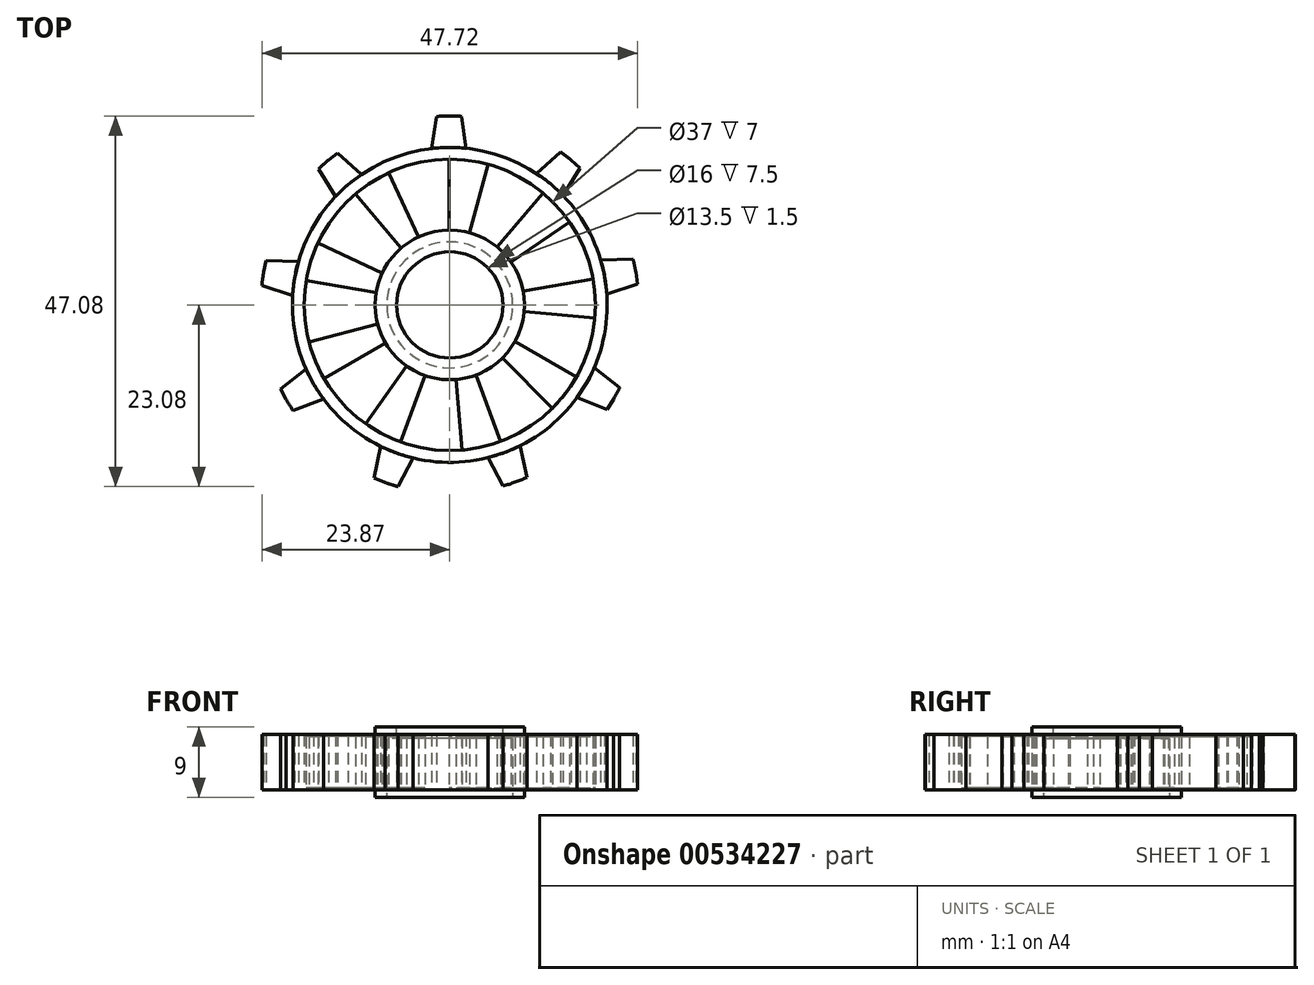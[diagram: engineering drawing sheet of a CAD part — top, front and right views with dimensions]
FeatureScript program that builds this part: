
annotation { "Feature Type Name" : "Feature", "Feature Type Description" : "" }
export const myFeature = defineFeature(function(context is Context, id is Id, definition is map)
    precondition{}
    {
        {
            var Q0;
            Q0=qCreatedBy(makeId("Top.planeOp"),FACE);
            var sketch = newSketch(context, id + "F0", { "sketchPlane" : qUnion([Q0])});
            skCircle(sketch, "E0", {"center": v(0, 0) * mm, "radius": 8 * mm});
            skCircle(sketch, "E1", {"center": v(0, 0) * mm, "radius": 9.5 * mm});
            skCircle(sketch, "E2", {"center": v(0, 0) * mm, "radius": 18.5 * mm});
            skCircle(sketch, "E3", {"center": v(0, 0) * mm, "radius": 20 * mm});
            skCircle(sketch, "E4", {"center": v(0, 0) * mm, "radius": 24 * mm});
            skLineSegment(sketch, "E5.trimOffspring", {"start": v(-0.1, 9.5) * mm, "end": v(-0.1, 18.5) * mm});
            skLineSegment(sketch, "E6", {"start": v(2.5, 9.17) * mm, "end": v(4.86, 17.85) * mm});
            skLineSegment(sketch, "E7.1.0", {"start": v(-6.18, 7.21) * mm, "end": v(-11.97, 14.1) * mm});
            skLineSegment(sketch, "E7.1.1", {"start": v(-3.98, 8.63) * mm, "end": v(-7.75, 16.8) * mm});
            skLineSegment(sketch, "E7.2.0", {"start": v(-9.37, 1.55) * mm, "end": v(-18.24, 3.11) * mm});
            skLineSegment(sketch, "E7.2.1", {"start": v(-8.6, 4.05) * mm, "end": v(-16.74, 7.88) * mm});
            skLineSegment(sketch, "E7.3.0", {"start": v(-8.18, -4.84) * mm, "end": v(-15.97, -9.34) * mm});
            skLineSegment(sketch, "E7.3.1", {"start": v(-9.19, -2.42) * mm, "end": v(-17.89, -4.72) * mm});
            skLineSegment(sketch, "E7.4.0", {"start": v(-3.15, -8.96) * mm, "end": v(-6.23, -17.42) * mm});
            skLineSegment(sketch, "E7.4.1", {"start": v(-5.48, -7.76) * mm, "end": v(-10.67, -15.11) * mm});
            skLineSegment(sketch, "E7.5.0", {"start": v(3.34, -8.9) * mm, "end": v(6.42, -17.35) * mm});
            skLineSegment(sketch, "E7.5.1", {"start": v(0.8, -9.47) * mm, "end": v(1.54, -18.44) * mm});
            skLineSegment(sketch, "E7.6.0", {"start": v(8.28, -4.66) * mm, "end": v(16.07, -9.16) * mm});
            skLineSegment(sketch, "E7.6.1", {"start": v(6.7, -6.74) * mm, "end": v(13.03, -13.13) * mm});
            skLineSegment(sketch, "E7.7.0", {"start": v(9.34, 1.75) * mm, "end": v(18.2, 3.31) * mm});
            skLineSegment(sketch, "E7.7.1", {"start": v(9.46, -0.86) * mm, "end": v(18.42, -1.68) * mm});
            skLineSegment(sketch, "E7.8.0", {"start": v(6.03, 7.34) * mm, "end": v(11.81, 14.24) * mm});
            skLineSegment(sketch, "E7.8.1", {"start": v(7.8, 5.42) * mm, "end": v(15.2, 10.55) * mm});
            skLineSegment(sketch, "E8", {"start": v(-1.7, 23.94) * mm, "end": v(-2.3, 19.87) * mm});
            skLineSegment(sketch, "E9", {"start": v(1.5, 23.95) * mm, "end": v(2.1, 19.89) * mm});
            skLineSegment(sketch, "E10.1.0", {"start": v(-15.57, 18.25) * mm, "end": v(-16.69, 17.25) * mm});
            skLineSegment(sketch, "E10.1.1", {"start": v(-16.69, 17.25) * mm, "end": v(-14.53, 13.74) * mm});
            skLineSegment(sketch, "E10.1.2", {"start": v(-15.43, 18.39) * mm, "end": v(-14.25, 19.31) * mm});
            skLineSegment(sketch, "E10.1.3", {"start": v(-12.92, 15.24) * mm, "end": v(-14.53, 13.74) * mm});
            skLineSegment(sketch, "E10.1.4", {"start": v(-14.25, 19.31) * mm, "end": v(-11.18, 16.58) * mm});
            skLineSegment(sketch, "E10.1.5", {"start": v(-12.93, 15.26) * mm, "end": v(-11.18, 16.58) * mm});
            skLineSegment(sketch, "E10.2.0", {"start": v(-23.66, 3.97) * mm, "end": v(-23.87, 2.48) * mm});
            skLineSegment(sketch, "E10.2.1", {"start": v(-23.87, 2.48) * mm, "end": v(-19.96, 1.19) * mm});
            skLineSegment(sketch, "E10.2.2", {"start": v(-23.64, 4.17) * mm, "end": v(-23.33, 5.64) * mm});
            skLineSegment(sketch, "E10.2.3", {"start": v(-19.7, 3.37) * mm, "end": v(-19.96, 1.19) * mm});
            skLineSegment(sketch, "E10.2.4", {"start": v(-23.33, 5.64) * mm, "end": v(-19.22, 5.52) * mm});
            skLineSegment(sketch, "E10.2.5", {"start": v(-19.71, 3.37) * mm, "end": v(-19.22, 5.52) * mm});
            skLineSegment(sketch, "E10.3.0", {"start": v(-20.67, -12.17) * mm, "end": v(-19.88, -13.44) * mm});
            skLineSegment(sketch, "E10.3.1", {"start": v(-19.88, -13.44) * mm, "end": v(-16.06, -11.92) * mm});
            skLineSegment(sketch, "E10.3.2", {"start": v(-20.78, -12) * mm, "end": v(-21.5, -10.68) * mm});
            skLineSegment(sketch, "E10.3.3", {"start": v(-17.25, -10.07) * mm, "end": v(-16.06, -11.92) * mm});
            skLineSegment(sketch, "E10.3.4", {"start": v(-21.5, -10.68) * mm, "end": v(-18.27, -8.13) * mm});
            skLineSegment(sketch, "E10.3.5", {"start": v(-17.27, -10.09) * mm, "end": v(-18.27, -8.13) * mm});
            skLineSegment(sketch, "E10.4.0", {"start": v(-8.02, -22.6) * mm, "end": v(-6.6, -23.08) * mm});
            skLineSegment(sketch, "E10.4.1", {"start": v(-6.6, -23.08) * mm, "end": v(-4.64, -19.45) * mm});
            skLineSegment(sketch, "E10.4.2", {"start": v(-8.2, -22.55) * mm, "end": v(-9.6, -22) * mm});
            skLineSegment(sketch, "E10.4.3", {"start": v(-6.74, -18.8) * mm, "end": v(-4.64, -19.45) * mm});
            skLineSegment(sketch, "E10.4.4", {"start": v(-9.6, -22) * mm, "end": v(-8.77, -17.97) * mm});
            skLineSegment(sketch, "E10.4.5", {"start": v(-6.75, -18.83) * mm, "end": v(-8.77, -17.97) * mm});
            skLineSegment(sketch, "E10.5.1", {"start": v(9.78, -21.92) * mm, "end": v(8.95, -17.88) * mm});
            skLineSegment(sketch, "E10.5.3", {"start": v(6.93, -18.74) * mm, "end": v(8.95, -17.88) * mm});
            skLineSegment(sketch, "E10.5.4", {"start": v(6.78, -23.02) * mm, "end": v(4.83, -19.4) * mm});
            skLineSegment(sketch, "E10.5.5", {"start": v(6.93, -18.76) * mm, "end": v(4.83, -19.4) * mm});
            skLineSegment(sketch, "E10.6.0", {"start": v(20.87, -11.82) * mm, "end": v(21.58, -10.5) * mm});
            skLineSegment(sketch, "E10.6.1", {"start": v(21.58, -10.5) * mm, "end": v(18.35, -7.95) * mm});
            skLineSegment(sketch, "E10.6.2", {"start": v(20.78, -12) * mm, "end": v(20, -13.27) * mm});
            skLineSegment(sketch, "E10.6.3", {"start": v(17.35, -9.9) * mm, "end": v(18.35, -7.95) * mm});
            skLineSegment(sketch, "E10.6.4", {"start": v(20, -13.27) * mm, "end": v(16.18, -11.76) * mm});
            skLineSegment(sketch, "E10.6.5", {"start": v(17.37, -9.91) * mm, "end": v(16.18, -11.76) * mm});
            skLineSegment(sketch, "E10.7.0", {"start": v(23.59, 4.36) * mm, "end": v(23.28, 5.83) * mm});
            skLineSegment(sketch, "E10.7.1", {"start": v(23.28, 5.83) * mm, "end": v(19.17, 5.71) * mm});
            skLineSegment(sketch, "E10.7.2", {"start": v(23.64, 4.17) * mm, "end": v(23.85, 2.68) * mm});
            skLineSegment(sketch, "E10.7.3", {"start": v(19.66, 3.57) * mm, "end": v(19.17, 5.71) * mm});
            skLineSegment(sketch, "E10.7.4", {"start": v(23.85, 2.68) * mm, "end": v(19.95, 1.39) * mm});
            skLineSegment(sketch, "E10.7.5", {"start": v(19.68, 3.57) * mm, "end": v(19.95, 1.39) * mm});
            skLineSegment(sketch, "E10.8.0", {"start": v(15.27, 18.5) * mm, "end": v(14.09, 19.43) * mm});
            skLineSegment(sketch, "E10.8.1", {"start": v(14.09, 19.43) * mm, "end": v(11.01, 16.7) * mm});
            skLineSegment(sketch, "E10.8.2", {"start": v(15.43, 18.39) * mm, "end": v(16.55, 17.39) * mm});
            skLineSegment(sketch, "E10.8.3", {"start": v(12.77, 15.37) * mm, "end": v(11.01, 16.7) * mm});
            skLineSegment(sketch, "E10.8.4", {"start": v(16.55, 17.39) * mm, "end": v(14.4, 13.89) * mm});
            skLineSegment(sketch, "E10.8.5", {"start": v(12.78, 15.39) * mm, "end": v(14.4, 13.89) * mm});
            skSolve(sketch);
        }
        {
            var Q0;
            Q0=makeQuery(id+"F0.imprint","IMPRINT",FACE,{"disambiguationData":[TD([[makeQuery(id+"F0.imprint","IMPRINT",EDGE,{"derivedFrom":sQuery(id+"F0.wireOp",EDGE,"E0")}),-1.0]])]});
            extrude(context, id + "F1", {"entities" : qUnion([Q0]), "endBound" : BoundingType.SYMMETRIC, "depth" : 9 * mm, "offsetDistance" : 25 * mm});
        }
        {
            var Q0;
            {var subQ11=sQuery(id+"F0.wireOp",EDGE,"KNoMOfHx-20VM-SqMY-RUze-EZyGc1flUTZU");Q0=makeQuery(id+"F0.imprint","IMPRINT",FACE,{"disambiguationData":[TD([[makeQuery(id+"F0.imprint","IMPRINT",EDGE,{"derivedFrom":subQ11}),-1.0]])]});}
            var Q1;
            {var subQ0=sQuery(id+"F0.wireOp",EDGE,"E7.1.0");Q1=makeQuery(id+"F0.imprint","IMPRINT",FACE,{"disambiguationData":[TD([[makeQuery(id+"F0.imprint","IMPRINT",EDGE,{"derivedFrom":subQ0}),-1.0]])]});}
            var Q2;
            {var subQ0=sQuery(id+"F0.wireOp",EDGE,"E5.trimOffspring");Q2=makeQuery(id+"F0.imprint","IMPRINT",FACE,{"disambiguationData":[TD([[makeQuery(id+"F0.imprint","IMPRINT",EDGE,{"derivedFrom":subQ0}),-1.0]])]});}
            var Q3;
            {var subQ0=sQuery(id+"F0.wireOp",EDGE,"E7.8.0");Q3=makeQuery(id+"F0.imprint","IMPRINT",FACE,{"disambiguationData":[TD([[makeQuery(id+"F0.imprint","IMPRINT",EDGE,{"derivedFrom":subQ0}),-1.0]])]});}
            var Q4;
            {var subQ0=sQuery(id+"F0.wireOp",EDGE,"E7.7.0");Q4=makeQuery(id+"F0.imprint","IMPRINT",FACE,{"disambiguationData":[TD([[makeQuery(id+"F0.imprint","IMPRINT",EDGE,{"derivedFrom":subQ0}),-1.0]])]});}
            var Q5;
            {var subQ0=sQuery(id+"F0.wireOp",EDGE,"E7.6.0");Q5=makeQuery(id+"F0.imprint","IMPRINT",FACE,{"disambiguationData":[TD([[makeQuery(id+"F0.imprint","IMPRINT",EDGE,{"derivedFrom":subQ0}),-1.0]])]});}
            var Q6;
            {var subQ0=sQuery(id+"F0.wireOp",EDGE,"E7.5.0");Q6=makeQuery(id+"F0.imprint","IMPRINT",FACE,{"disambiguationData":[TD([[makeQuery(id+"F0.imprint","IMPRINT",EDGE,{"derivedFrom":subQ0}),-1.0]])]});}
            var Q7;
            {var subQ0=sQuery(id+"F0.wireOp",EDGE,"E7.4.0");Q7=makeQuery(id+"F0.imprint","IMPRINT",FACE,{"disambiguationData":[TD([[makeQuery(id+"F0.imprint","IMPRINT",EDGE,{"derivedFrom":subQ0}),-1.0]])]});}
            var Q8;
            {var subQ0=sQuery(id+"F0.wireOp",EDGE,"E7.3.0");Q8=makeQuery(id+"F0.imprint","IMPRINT",FACE,{"disambiguationData":[TD([[makeQuery(id+"F0.imprint","IMPRINT",EDGE,{"derivedFrom":subQ0}),-1.0]])]});}
            var Q9;
            {var subQ0=sQuery(id+"F0.wireOp",EDGE,"E7.2.0");Q9=makeQuery(id+"F0.imprint","IMPRINT",FACE,{"disambiguationData":[TD([[makeQuery(id+"F0.imprint","IMPRINT",EDGE,{"derivedFrom":subQ0}),-1.0]])]});}
            extrude(context, id + "F2", {"entities" : qUnion([Q0, Q1, Q2, Q3, Q4, Q5, Q6, Q7, Q8, Q9]), "endBound" : BoundingType.SYMMETRIC, "depth" : 6.5 * mm, "offsetDistance" : 25 * mm});
        }
        {
            var Q0;
            {var subQ0=sQuery(id+"F0.wireOp",EDGE,"E8");Q0=makeQuery(id+"F0.imprint","IMPRINT",FACE,{"disambiguationData":[TD([[makeQuery(id+"F0.imprint","IMPRINT",EDGE,{"derivedFrom":subQ0}),1.0]])]});}
            var Q1;
            {var subQ0=sQuery(id+"F0.wireOp",EDGE,"E10.8.1");Q1=makeQuery(id+"F0.imprint","IMPRINT",FACE,{"disambiguationData":[TD([[makeQuery(id+"F0.imprint","IMPRINT",EDGE,{"derivedFrom":subQ0}),1.0]])]});}
            var Q2;
            {var subQ0=sQuery(id+"F0.wireOp",EDGE,"E10.7.1");Q2=makeQuery(id+"F0.imprint","IMPRINT",FACE,{"disambiguationData":[TD([[makeQuery(id+"F0.imprint","IMPRINT",EDGE,{"derivedFrom":subQ0}),1.0]])]});}
            var Q3;
            {var subQ0=sQuery(id+"F0.wireOp",EDGE,"E10.6.1");Q3=makeQuery(id+"F0.imprint","IMPRINT",FACE,{"disambiguationData":[TD([[makeQuery(id+"F0.imprint","IMPRINT",EDGE,{"derivedFrom":subQ0}),1.0]])]});}
            var Q4;
            {var subQ0=sQuery(id+"F0.wireOp",EDGE,"E10.6.1");Q4=makeQuery(id+"F0.imprint","IMPRINT",FACE,{"disambiguationData":[TD([[makeQuery(id+"F0.imprint","IMPRINT",EDGE,{"derivedFrom":subQ0}),1.0]])]});}
            var Q5;
            {var subQ0=sQuery(id+"F0.wireOp",EDGE,"E10.5.1");Q5=makeQuery(id+"F0.imprint","IMPRINT",FACE,{"disambiguationData":[TD([[makeQuery(id+"F0.imprint","IMPRINT",EDGE,{"derivedFrom":subQ0}),1.0]])]});}
            var Q6;
            {var subQ0=sQuery(id+"F0.wireOp",EDGE,"E10.4.1");Q6=makeQuery(id+"F0.imprint","IMPRINT",FACE,{"disambiguationData":[TD([[makeQuery(id+"F0.imprint","IMPRINT",EDGE,{"derivedFrom":subQ0}),1.0]])]});}
            var Q7;
            {var subQ0=sQuery(id+"F0.wireOp",EDGE,"E10.3.1");Q7=makeQuery(id+"F0.imprint","IMPRINT",FACE,{"disambiguationData":[TD([[makeQuery(id+"F0.imprint","IMPRINT",EDGE,{"derivedFrom":subQ0}),1.0]])]});}
            var Q8;
            {var subQ0=sQuery(id+"F0.wireOp",EDGE,"E10.2.1");Q8=makeQuery(id+"F0.imprint","IMPRINT",FACE,{"disambiguationData":[TD([[makeQuery(id+"F0.imprint","IMPRINT",EDGE,{"derivedFrom":subQ0}),1.0]])]});}
            var Q9;
            {var subQ0=sQuery(id+"F0.wireOp",EDGE,"E10.1.1");Q9=makeQuery(id+"F0.imprint","IMPRINT",FACE,{"disambiguationData":[TD([[makeQuery(id+"F0.imprint","IMPRINT",EDGE,{"derivedFrom":subQ0}),1.0]])]});}
            extrude(context, id + "F3", {"entities" : qUnion([Q0, Q1, Q2, Q3, Q4, Q5, Q6, Q7, Q8, Q9]), "endBound" : BoundingType.SYMMETRIC, "depth" : 7 * mm, "offsetDistance" : 25 * mm});
        }
        {
            var Q0;
            {var subQ31=sQuery(id+"F0.wireOp",EDGE,"E10.1.5");Q0=makeQuery(id+"F0.imprint","IMPRINT",FACE,{"disambiguationData":[TD([[makeQuery(id+"F0.imprint","IMPRINT",EDGE,{"derivedFrom":subQ31}),-1.0]])]});}
            extrude(context, id + "F4", {"entities" : qUnion([Q0]), "endBound" : BoundingType.SYMMETRIC, "depth" : 7 * mm, "offsetDistance" : 25 * mm});
        }
        {
            var Q0;
            Q0=makeQuery(id+"F1.opExtrude","CAP_FACE",FACE,{"disambiguationData":[OSD([sQuery(id+"F0.wireOp",EDGE,"E0"),sQuery(id+"F0.wireOp",EDGE,"E1")])],"isStart":false});
            var sketch = newSketch(context, id + "F5", { "sketchPlane" : qUnion([Q0])});
            skCircle(sketch, "E11", {"center": v(0, 0) * mm, "radius": 6.75 * mm});
            skSolve(sketch);
        }
        {
            var Q0;
            Q0=makeQuery(id+"F5.imprint","IMPRINT",FACE,{"disambiguationData":[TD([[makeQuery(id+"F5.imprint","IMPRINT",EDGE,{"derivedFrom":sQuery(id+"F5.wireOp",EDGE,"E11")}),-1.0]])]});
            extrude(context, id + "F6", {"entities" : qUnion([Q0]), "operationType" : NewBodyOperationType.ADD, "oppositeDirection" : true, "depth" : 1.5 * mm, "offsetDistance" : 25 * mm});
        }
    });
